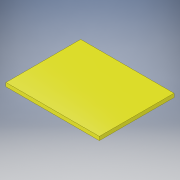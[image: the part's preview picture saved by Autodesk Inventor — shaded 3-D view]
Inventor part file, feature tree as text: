
AUTODESK INVENTOR PART (.ipt)
format: ipt  version: 2019.4 (Build 234330000, 330)  size: 126,976 bytes
history: native  units: in
note: dims shown in document units (in); Inventor stores cm internally (conversion verified against a paired STEP export)
features: sketch x2, extrude x1
ambient origin geometry x8: Origin, YZ Plane, XZ Plane, XY Plane, X Axis, Y Axis, Z Axis, Center Point
bodies: Solid1 (feature_tree)
feature tree (3):
  extrude  "Extrusion1"  Depth=4.0in
  sketch  "Sketch1"  dims[d0=5.0in d1=4.0in]
  sketch  "Sketch22"  dims[d2=0.2in d3=0.0in]
